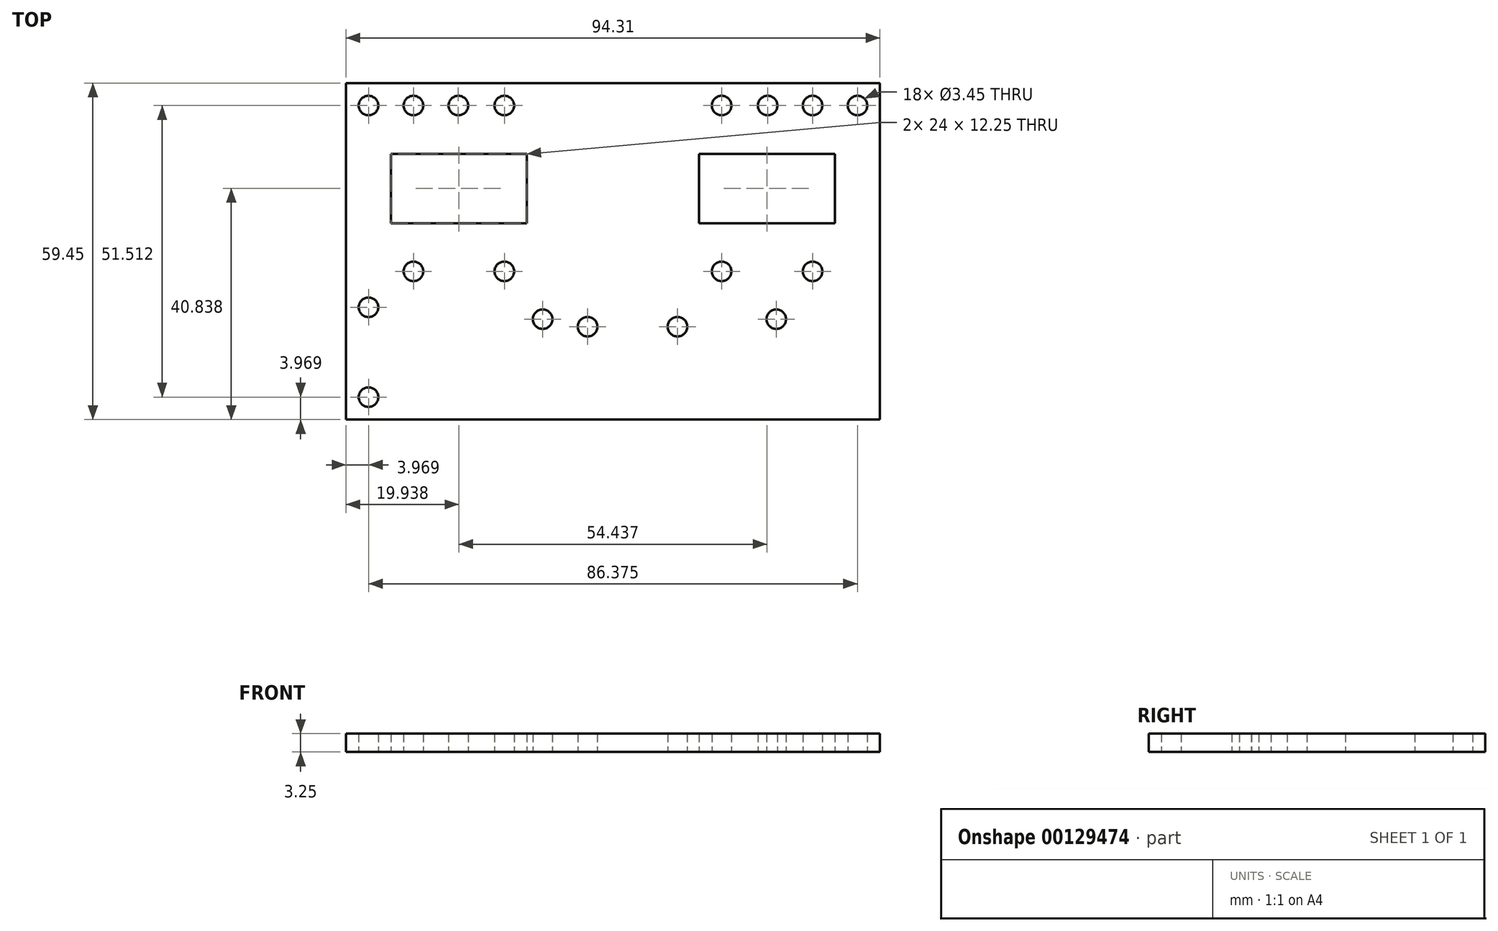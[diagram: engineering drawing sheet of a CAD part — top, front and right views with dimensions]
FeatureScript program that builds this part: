
annotation { "Feature Type Name" : "Feature", "Feature Type Description" : "" }
export const myFeature = defineFeature(function(context is Context, id is Id, definition is map)
    precondition{}
    {
        {
            var Q0;
            Q0=qCreatedBy(makeId("Top.planeOp"),FACE);
            var sketch = newSketch(context, id + "F0", { "sketchPlane" : qUnion([Q0])});
            skLineSegment(sketch, "E0.bottom", {"start": v(0, 0) * mm, "end": v(94.31, 0) * mm});
            skLineSegment(sketch, "E0.top", {"start": v(0, -59.45) * mm, "end": v(94.31, -59.45) * mm});
            skLineSegment(sketch, "E0.left", {"start": v(0, 0) * mm, "end": v(0, -59.45) * mm});
            skLineSegment(sketch, "E0.right", {"start": v(94.31, 0) * mm, "end": v(94.31, -59.45) * mm});
            skLineSegment(sketch, "E1.bottom", {"start": v(7.94, -12.49) * mm, "end": v(31.94, -12.49) * mm});
            skLineSegment(sketch, "E2.bottom", {"start": v(86.37, -12.49) * mm, "end": v(62.37, -12.49) * mm});
            skLineSegment(sketch, "E1.top", {"start": v(7.94, -24.74) * mm, "end": v(31.94, -24.74) * mm});
            skPoint(sketch, "E3.rect.middle", {"position": v(47.16, -18.61) * mm});
            skLineSegment(sketch, "E2.top", {"start": v(86.37, -24.74) * mm, "end": v(62.37, -24.74) * mm});
            skLineSegment(sketch, "E4", {"start": v(31.94, -18.61) * mm, "end": v(62.37, -18.61) * mm, "construction": true});
            skLineSegment(sketch, "E1.left", {"start": v(7.94, -12.49) * mm, "end": v(7.94, -24.74) * mm});
            skLineSegment(sketch, "E2.right", {"start": v(62.37, -12.49) * mm, "end": v(62.37, -24.74) * mm});
            skLineSegment(sketch, "E5", {"start": v(0, -18.61) * mm, "end": v(7.94, -18.61) * mm, "construction": true});
            skLineSegment(sketch, "E1.right", {"start": v(31.94, -12.49) * mm, "end": v(31.94, -24.74) * mm});
            skLineSegment(sketch, "E2.left", {"start": v(86.37, -12.49) * mm, "end": v(86.37, -24.74) * mm});
            skLineSegment(sketch, "E6", {"start": v(86.37, -18.61) * mm, "end": v(94.31, -18.61) * mm});
            skPoint(sketch, "E6.endSnap0", {"position": v(86.37, -18.61) * mm});
            skCircle(sketch, "E7", {"center": v(34.73, -41.71) * mm, "radius": 1.73 * mm});
            skCircle(sketch, "E8", {"center": v(76, -41.71) * mm, "radius": 1.73 * mm});
            skLineSegment(sketch, "E9", {"start": v(47.16, -43.03) * mm, "end": v(47.16, -33.5) * mm, "construction": true});
            skLineSegment(sketch, "E10", {"start": v(42.67, -43.03) * mm, "end": v(58.55, -43.03) * mm, "construction": true});
            skCircle(sketch, "E11", {"center": v(42.67, -43.03) * mm, "radius": 1.73 * mm});
            skCircle(sketch, "E12", {"center": v(58.55, -43.03) * mm, "radius": 1.73 * mm});
            skLineSegment(sketch, "E13.rect.left", {"start": v(11.9, -3.97) * mm, "end": v(11.9, -33.26) * mm, "construction": true});
            skLineSegment(sketch, "E13.rect.right", {"start": v(82.4, -3.97) * mm, "end": v(82.4, -33.26) * mm, "construction": true});
            skLineSegment(sketch, "E14.bottom", {"start": v(11.9, -3.97) * mm, "end": v(7.94, -3.97) * mm, "construction": true});
            skLineSegment(sketch, "E14.left", {"start": v(11.9, -3.97) * mm, "end": v(11.9, 0) * mm, "construction": true});
            skLineSegment(sketch, "E15", {"start": v(7.94, -12.49) * mm, "end": v(7.94, -3.97) * mm, "construction": true});
            skCircle(sketch, "E16", {"center": v(11.9, -3.97) * mm, "radius": 1.73 * mm});
            skCircle(sketch, "E17", {"center": v(11.9, -33.26) * mm, "radius": 1.73 * mm});
            skCircle(sketch, "E18", {"center": v(82.4, -33.26) * mm, "radius": 1.73 * mm});
            skCircle(sketch, "E19", {"center": v(82.4, -3.97) * mm, "radius": 1.73 * mm});
            skLineSegment(sketch, "E20", {"start": v(0, -3.97) * mm, "end": v(3.97, -3.97) * mm, "construction": true});
            skLineSegment(sketch, "E21", {"start": v(3.97, -3.97) * mm, "end": v(3.97, 0) * mm, "construction": true});
            skLineSegment(sketch, "E22", {"start": v(3.97, -3.97) * mm, "end": v(19.84, -3.97) * mm, "construction": true});
            skCircle(sketch, "E23", {"center": v(3.97, -3.97) * mm, "radius": 1.73 * mm});
            skCircle(sketch, "E24", {"center": v(19.84, -3.97) * mm, "radius": 1.73 * mm});
            skLineSegment(sketch, "E25", {"start": v(94.31, -3.97) * mm, "end": v(90.34, -3.97) * mm, "construction": true});
            skLineSegment(sketch, "E26", {"start": v(90.34, -3.97) * mm, "end": v(74.47, -3.97) * mm, "construction": true});
            skCircle(sketch, "E27", {"center": v(74.47, -3.97) * mm, "radius": 1.73 * mm});
            skCircle(sketch, "E28", {"center": v(90.34, -3.97) * mm, "radius": 1.73 * mm});
            skLineSegment(sketch, "E29", {"start": v(34.73, -41.71) * mm, "end": v(76, -41.71) * mm, "construction": true});
            skLineSegment(sketch, "E30", {"start": v(47.16, -29.13) * mm, "end": v(47.16, -43.03) * mm, "construction": true});
            skLineSegment(sketch, "E31", {"start": v(47.16, -41.71) * mm, "end": v(47.16, -59.45) * mm, "construction": true});
            skLineSegment(sketch, "E32", {"start": v(0, -55.48) * mm, "end": v(3.97, -55.48) * mm, "construction": true});
            skLineSegment(sketch, "E33", {"start": v(3.97, -55.48) * mm, "end": v(3.97, -59.45) * mm, "construction": true});
            skLineSegment(sketch, "E34", {"start": v(3.97, -55.48) * mm, "end": v(3.97, -39.6) * mm, "construction": true});
            skCircle(sketch, "E35", {"center": v(3.97, -39.6) * mm, "radius": 1.73 * mm});
            skCircle(sketch, "E36", {"center": v(3.97, -55.48) * mm, "radius": 1.73 * mm});
            skLineSegment(sketch, "E37", {"start": v(34.73, -41.71) * mm, "end": v(0, -41.71) * mm, "construction": true});
            skLineSegment(sketch, "E38", {"start": v(76, -41.71) * mm, "end": v(94.31, -41.71) * mm, "construction": true});
            skLineSegment(sketch, "E39", {"start": v(34.73, -41.71) * mm, "end": v(34.73, -43.03) * mm, "construction": true});
            skLineSegment(sketch, "E40", {"start": v(34.73, -43.03) * mm, "end": v(42.67, -43.03) * mm, "construction": true});
            skLineSegment(sketch, "E41", {"start": v(11.9, -33.26) * mm, "end": v(27.97, -33.26) * mm, "construction": true});
            skLineSegment(sketch, "E42", {"start": v(82.4, -33.26) * mm, "end": v(66.34, -33.26) * mm, "construction": true});
            skCircle(sketch, "E43", {"center": v(27.97, -33.26) * mm, "radius": 1.73 * mm});
            skCircle(sketch, "E44", {"center": v(66.34, -33.26) * mm, "radius": 1.73 * mm});
            skLineSegment(sketch, "E45", {"start": v(27.97, -33.26) * mm, "end": v(27.97, -3.97) * mm, "construction": true});
            skLineSegment(sketch, "E46", {"start": v(19.84, -3.97) * mm, "end": v(27.97, -3.97) * mm, "construction": true});
            skLineSegment(sketch, "E47", {"start": v(74.47, -3.97) * mm, "end": v(66.34, -3.97) * mm, "construction": true});
            skLineSegment(sketch, "E48", {"start": v(66.34, -33.26) * mm, "end": v(66.34, -3.97) * mm, "construction": true});
            skCircle(sketch, "E49", {"center": v(66.34, -3.97) * mm, "radius": 1.73 * mm});
            skCircle(sketch, "E50", {"center": v(27.97, -3.97) * mm, "radius": 1.73 * mm});
            skSolve(sketch);
        }
        {
            var Q0;
            Q0=qSketchRegion(id+"F0",true);
            extrude(context, id + "F1", {"entities" : qUnion([Q0]), "depth" : 3.25 * mm});
        }
    });
